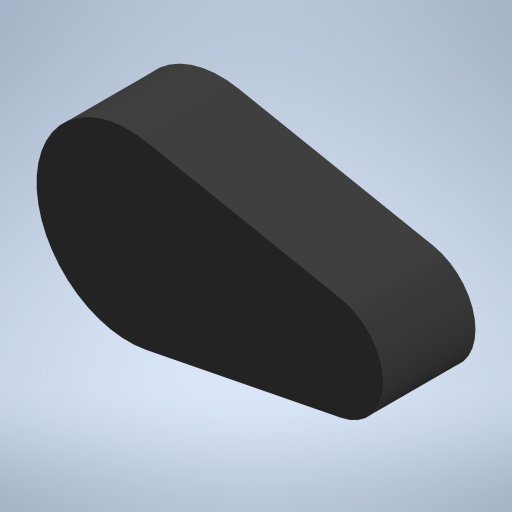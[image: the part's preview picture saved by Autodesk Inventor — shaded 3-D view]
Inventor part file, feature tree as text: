
AUTODESK INVENTOR PART (.ipt)
format: ipt  version: 2023 (Build 270158000, 158)  size: 205,312 bytes
history: native  units: in
note: dims shown in document units (in); Inventor stores cm internally (conversion verified against a paired STEP export)
features: extrude x1, sketch x1
ambient origin geometry x8: Origin, YZ Plane, XZ Plane, XY Plane, X Axis, Y Axis, Z Axis, Center Point
bodies: Solid1 (feature_tree)
feature tree (2):
  extrude  "Extrusion1"  Depth=1.378in
  sketch  "Sketch1"  dims[d0=2.7559in d2=1.5748in d3=0.0in d4=5.2005in d5=1.378in d6=0.0in]
